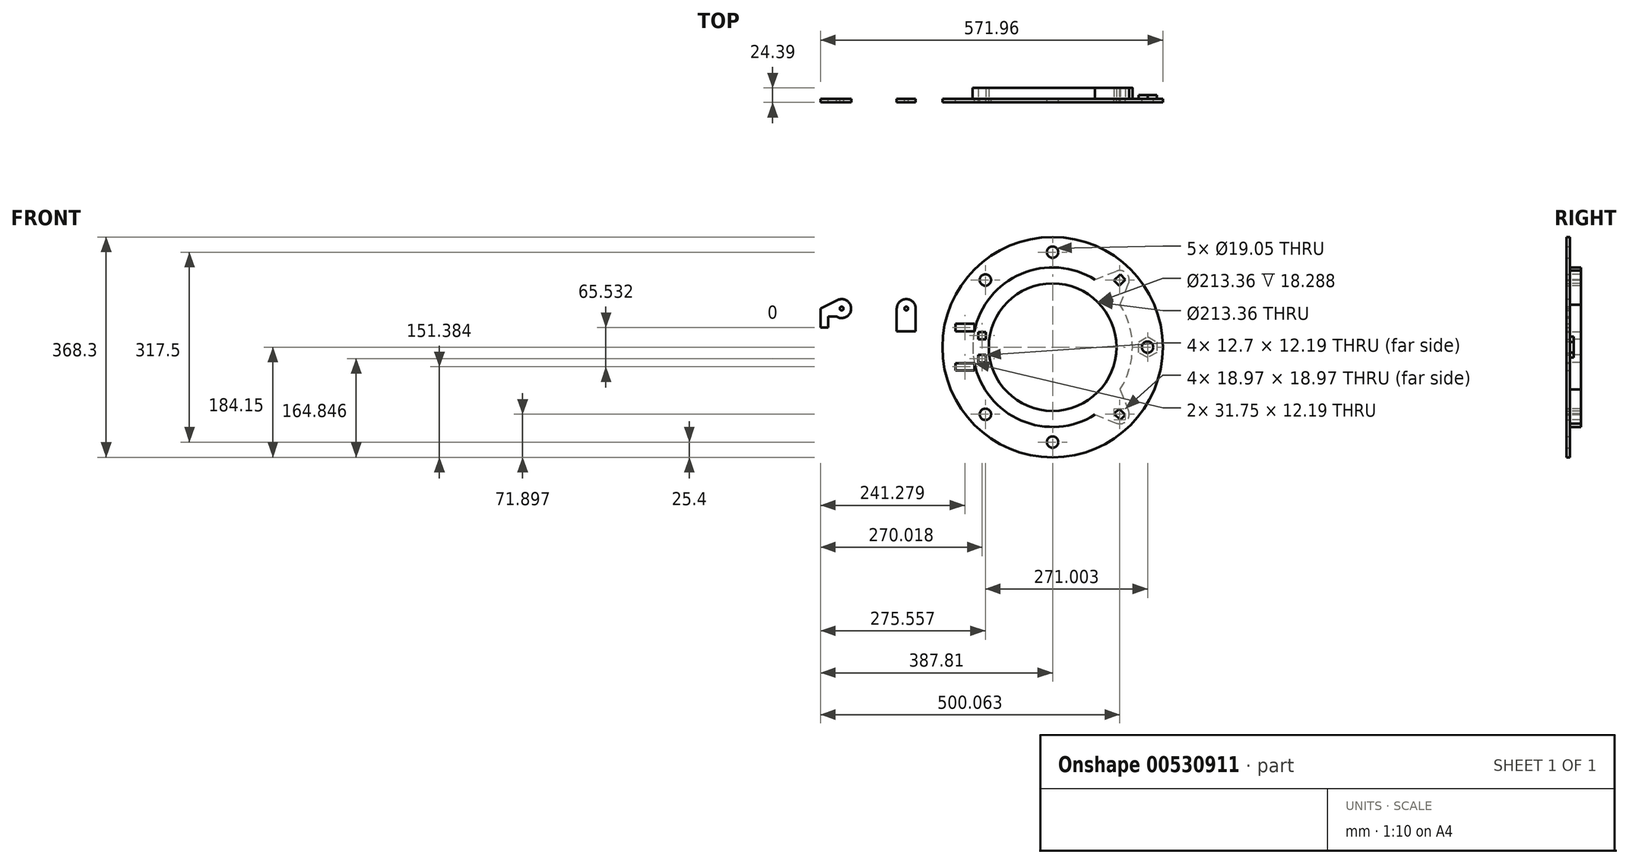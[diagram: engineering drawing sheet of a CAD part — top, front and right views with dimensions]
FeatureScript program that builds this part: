
annotation { "Feature Type Name" : "Feature", "Feature Type Description" : "" }
export const myFeature = defineFeature(function(context is Context, id is Id, definition is map)
    precondition{}
    {
        {
            var Q0;
            Q0=qCreatedBy(makeId("Front.planeOp"),FACE);
            var sketch = newSketch(context, id + "F0", { "sketchPlane" : qUnion([Q0])});
            skCircle(sketch, "E0", {"center": v(0, 0) * mm, "radius": 114.3 * mm, "construction": true});
            skArc(sketch, "E1", {"start": v(70.98, 112.89) * mm, "mid": v(-133.35, 0) * mm, "end": v(70.98, -112.89) * mm});
            skCircle(sketch, "E2", {"center": v(0, 0) * mm, "radius": 184.15 * mm});
            skCircle(sketch, "E3", {"center": v(0, 158.75) * mm, "radius": 9.53 * mm});
            skLineSegment(sketch, "E4", {"start": v(0, 133.35) * mm, "end": v(0, 184.15) * mm, "construction": true});
            skCircle(sketch, "E5.1.0", {"center": v(-112.25, 112.25) * mm, "radius": 9.53 * mm});
            skCircle(sketch, "E5.3.0", {"center": v(-112.25, -112.25) * mm, "radius": 9.53 * mm});
            skCircle(sketch, "E5.4.0", {"center": v(0, -158.75) * mm, "radius": 9.52 * mm});
            skCircle(sketch, "E5.5.0", {"center": v(112.25, -112.25) * mm, "radius": 9.53 * mm, "construction": true});
            skCircle(sketch, "E5.6.0", {"center": v(158.75, 0) * mm, "radius": 9.53 * mm});
            skCircle(sketch, "E5.7.0", {"center": v(112.25, 112.25) * mm, "radius": 9.53 * mm, "construction": true});
            skLineSegment(sketch, "E6", {"start": v(-133.35, 0) * mm, "end": v(-184.15, 0) * mm, "construction": true});
            skLineSegment(sketch, "E7.bottom", {"start": v(-162.4, 38.86) * mm, "end": v(-130.66, 38.86) * mm});
            skLineSegment(sketch, "E7.top", {"start": v(-162.4, 26.67) * mm, "end": v(-130.66, 26.67) * mm});
            skLineSegment(sketch, "E7.left", {"start": v(-162.4, 38.86) * mm, "end": v(-162.4, 26.67) * mm});
            skLineSegment(sketch, "E7.right", {"start": v(-130.66, 38.86) * mm, "end": v(-130.66, 26.67) * mm});
            skLineSegment(sketch, "E8.MirrorCS", {"start": v(-130.66, -38.86) * mm, "end": v(-130.66, -26.67) * mm});
            skLineSegment(sketch, "E9.MirrorCS", {"start": v(-162.4, -38.86) * mm, "end": v(-162.4, -26.67) * mm});
            skLineSegment(sketch, "E10.MirrorCS", {"start": v(-162.4, -26.67) * mm, "end": v(-130.66, -26.67) * mm});
            skLineSegment(sketch, "E11.MirrorCS", {"start": v(-162.4, -38.86) * mm, "end": v(-130.66, -38.86) * mm});
            skLineSegment(sketch, "E12", {"start": v(-228.6, 26.67) * mm, "end": v(-260.35, 26.67) * mm});
            skLineSegment(sketch, "E13", {"start": v(-260.35, 26.67) * mm, "end": v(-260.35, 64.52) * mm});
            skArc(sketch, "E14", {"start": v(-228.6, 64.52) * mm, "mid": v(-244.47, 80.4) * mm, "end": v(-260.35, 64.52) * mm});
            skPoint(sketch, "E14.centerSnap0", {"position": v(-244.48, 26.67) * mm});
            skLineSegment(sketch, "E15", {"start": v(-228.6, 26.67) * mm, "end": v(-228.6, 64.52) * mm});
            skLineSegment(sketch, "E16.bottom", {"start": v(-228.6, 26.67) * mm, "end": v(-203.2, 26.67) * mm, "construction": true});
            skLineSegment(sketch, "E16.top", {"start": v(-228.6, 51.05) * mm, "end": v(-203.2, 51.05) * mm, "construction": true});
            skLineSegment(sketch, "E16.left", {"start": v(-228.6, 26.67) * mm, "end": v(-228.6, 51.05) * mm, "construction": true});
            skLineSegment(sketch, "E16.right", {"start": v(-203.2, 26.67) * mm, "end": v(-203.2, 51.05) * mm, "construction": true});
            skLineSegment(sketch, "E17", {"start": v(-298.45, 64.52) * mm, "end": v(-298.45, 26.67) * mm, "construction": true});
            skLineSegment(sketch, "E18.MirrorCS", {"start": v(-368.3, 26.67) * mm, "end": v(-368.3, 64.52) * mm, "construction": true});
            skLineSegment(sketch, "E19.MirrorCS", {"start": v(-368.3, 26.67) * mm, "end": v(-368.3, 51.05) * mm, "construction": true});
            skLineSegment(sketch, "E20.MirrorCS", {"start": v(-368.3, 26.67) * mm, "end": v(-336.55, 26.67) * mm, "construction": true});
            skArc(sketch, "E21.MirrorCS", {"start": v(-359.55, 78.7) * mm, "mid": v(-344.09, 78.03) * mm, "end": v(-336.55, 64.52) * mm, "construction": true});
            skLineSegment(sketch, "E22.MirrorCS", {"start": v(-368.3, 51.05) * mm, "end": v(-393.7, 51.05) * mm, "construction": true});
            skLineSegment(sketch, "E23.MirrorCS", {"start": v(-393.7, 26.67) * mm, "end": v(-393.7, 51.05) * mm, "construction": true});
            skLineSegment(sketch, "E24.MirrorCS", {"start": v(-336.55, 26.67) * mm, "end": v(-336.55, 64.52) * mm, "construction": true});
            skPoint(sketch, "E25.MirrorP", {"position": v(-352.43, 26.67) * mm});
            skLineSegment(sketch, "E26.MirrorCS", {"start": v(-368.3, 26.67) * mm, "end": v(-393.7, 26.67) * mm, "construction": true});
            skArc(sketch, "E27", {"start": v(-360.84, 51.05) * mm, "mid": v(-336.57, 63.78) * mm, "end": v(-359.55, 78.7) * mm});
            skLineSegment(sketch, "E28", {"start": v(-130.66, 26.67) * mm, "end": v(-111.14, 26.67) * mm, "construction": true});
            skLineSegment(sketch, "E29", {"start": v(-368.3, 64.52) * mm, "end": v(-387.81, 64.52) * mm, "construction": true});
            skLineSegment(sketch, "E30", {"start": v(-387.81, 51.05) * mm, "end": v(-387.81, 64.52) * mm});
            skLineSegment(sketch, "E31", {"start": v(-387.81, 64.52) * mm, "end": v(-359.55, 78.7) * mm});
            skLineSegment(sketch, "E32", {"start": v(-387.81, 51.05) * mm, "end": v(-387.81, 32.77) * mm});
            skLineSegment(sketch, "E33", {"start": v(-387.81, 32.77) * mm, "end": v(-375.24, 32.77) * mm});
            skLineSegment(sketch, "E34", {"start": v(-375.24, 32.77) * mm, "end": v(-375.24, 51.05) * mm});
            skLineSegment(sketch, "E35", {"start": v(-375.24, 51.05) * mm, "end": v(-360.84, 51.05) * mm});
            skCircle(sketch, "E36.0", {"center": v(0, 0) * mm, "radius": 106.68 * mm});
            skLineSegment(sketch, "E37.bottom", {"start": v(-111.44, 25.4) * mm, "end": v(-124.14, 25.4) * mm});
            skLineSegment(sketch, "E37.top", {"start": v(-111.44, 13.2) * mm, "end": v(-124.14, 13.2) * mm});
            skLineSegment(sketch, "E37.left", {"start": v(-111.44, 25.4) * mm, "end": v(-111.44, 13.2) * mm});
            skLineSegment(sketch, "E37.right", {"start": v(-124.14, 25.4) * mm, "end": v(-124.14, 13.2) * mm});
            skLineSegment(sketch, "E38", {"start": v(0, 0) * mm, "end": v(112.25, 112.25) * mm, "construction": true});
            skLineSegment(sketch, "E39", {"start": v(0, 0) * mm, "end": v(112.25, -112.25) * mm, "construction": true});
            skArc(sketch, "E40", {"start": v(127, 106.37) * mm, "mid": v(123.48, 123.48) * mm, "end": v(106.37, 127) * mm});
            skLineSegment(sketch, "E41", {"start": v(70.98, 112.89) * mm, "end": v(106.37, 127) * mm});
            skLineSegment(sketch, "E42.MirrorCS", {"start": v(112.89, 70.98) * mm, "end": v(127, 106.37) * mm});
            skLineSegment(sketch, "E43.MirrorCS", {"start": v(70.98, -112.89) * mm, "end": v(106.37, -127) * mm});
            skArc(sketch, "E44.MirrorCS", {"start": v(127, -106.37) * mm, "mid": v(123.48, -123.48) * mm, "end": v(106.37, -127) * mm});
            skLineSegment(sketch, "E45.MirrorCS", {"start": v(112.89, -70.98) * mm, "end": v(127, -106.37) * mm});
            skArc(sketch, "E46.trimOffspring", {"start": v(112.89, -70.98) * mm, "mid": v(133.35, 0) * mm, "end": v(112.89, 70.98) * mm});
            skCircle(sketch, "E47.cCircle", {"center": v(158.75, 0) * mm, "radius": 15.24 * mm, "construction": true});
            skLineSegment(sketch, "E47.0", {"start": v(174, 8.8) * mm, "end": v(174, -8.8) * mm});
            skLineSegment(sketch, "E47.1", {"start": v(174, -8.8) * mm, "end": v(158.75, -17.6) * mm});
            skLineSegment(sketch, "E47.2", {"start": v(158.75, -17.6) * mm, "end": v(143.5, -8.8) * mm});
            skLineSegment(sketch, "E47.3", {"start": v(143.5, -8.8) * mm, "end": v(143.5, 8.8) * mm});
            skLineSegment(sketch, "E47.4", {"start": v(143.5, 8.8) * mm, "end": v(158.75, 17.6) * mm});
            skLineSegment(sketch, "E47.5", {"start": v(158.75, 17.6) * mm, "end": v(174, 8.8) * mm});
            skPoint(sketch, "E47.0.midPoint", {"position": v(174, 0) * mm});
            skArc(sketch, "E48", {"start": v(70.98, 112.89) * mm, "mid": v(94.3, 94.3) * mm, "end": v(112.89, 70.98) * mm});
            skArc(sketch, "E49", {"start": v(70.98, -112.89) * mm, "mid": v(94.3, -94.3) * mm, "end": v(112.89, -70.98) * mm});
            skLineSegment(sketch, "E50.MirrorCS", {"start": v(-124.14, -25.4) * mm, "end": v(-124.14, -13.2) * mm});
            skLineSegment(sketch, "E51.MirrorCS", {"start": v(-111.44, -25.4) * mm, "end": v(-111.44, -13.2) * mm});
            skLineSegment(sketch, "E52.MirrorCS", {"start": v(-111.44, -25.4) * mm, "end": v(-124.14, -25.4) * mm});
            skLineSegment(sketch, "E53.MirrorCS", {"start": v(-111.44, -13.2) * mm, "end": v(-124.14, -13.2) * mm});
            skLineSegment(sketch, "E54", {"start": v(102.77, 111.39) * mm, "end": v(111.39, 102.77) * mm});
            skLineSegment(sketch, "E55", {"start": v(102.77, 111.39) * mm, "end": v(113.12, 121.74) * mm});
            skLineSegment(sketch, "E56", {"start": v(113.12, 121.74) * mm, "end": v(121.74, 113.12) * mm});
            skLineSegment(sketch, "E57", {"start": v(121.74, 113.12) * mm, "end": v(111.39, 102.77) * mm});
            skLineSegment(sketch, "E58.MirrorCS", {"start": v(113.12, -121.74) * mm, "end": v(121.74, -113.12) * mm});
            skLineSegment(sketch, "E59.MirrorCS", {"start": v(102.77, -111.39) * mm, "end": v(113.12, -121.74) * mm});
            skLineSegment(sketch, "E60", {"start": v(102.77, -111.39) * mm, "end": v(111.39, -102.77) * mm});
            skLineSegment(sketch, "E61", {"start": v(111.39, -102.77) * mm, "end": v(121.74, -113.12) * mm});
            skLineSegment(sketch, "E62.bottom", {"start": v(152.4, 176.78) * mm, "end": v(166.62, 176.78) * mm});
            skLineSegment(sketch, "E62.top", {"start": v(152.4, 152.4) * mm, "end": v(166.62, 152.4) * mm});
            skLineSegment(sketch, "E62.left", {"start": v(152.4, 176.78) * mm, "end": v(152.4, 152.4) * mm});
            skLineSegment(sketch, "E62.right", {"start": v(166.62, 176.78) * mm, "end": v(166.62, 152.4) * mm});
            skLineSegment(sketch, "E63", {"start": v(166.62, 176.78) * mm, "end": v(204.72, 202.18) * mm});
            skLineSegment(sketch, "E64", {"start": v(159.51, 176.78) * mm, "end": v(159.51, 152.4) * mm, "construction": true});
            skLineSegment(sketch, "E65", {"start": v(204.72, 202.18) * mm, "end": v(204.72, 214.88) * mm});
            skLineSegment(sketch, "E66", {"start": v(204.72, 214.88) * mm, "end": v(179.32, 214.88) * mm});
            skLineSegment(sketch, "E67", {"start": v(179.32, 214.88) * mm, "end": v(159.51, 201.68) * mm});
            skLineSegment(sketch, "E68.MirrorCS", {"start": v(139.7, 214.88) * mm, "end": v(159.51, 201.68) * mm});
            skLineSegment(sketch, "E69.MirrorCS", {"start": v(114.3, 214.88) * mm, "end": v(139.7, 214.88) * mm});
            skLineSegment(sketch, "E70.MirrorCS", {"start": v(114.3, 202.18) * mm, "end": v(114.3, 214.88) * mm});
            skLineSegment(sketch, "E71.MirrorCS", {"start": v(152.4, 176.78) * mm, "end": v(114.3, 202.18) * mm});
            skCircle(sketch, "E72", {"center": v(-244.47, 64.52) * mm, "radius": 3.18 * mm});
            skCircle(sketch, "E73", {"center": v(-352.43, 64.52) * mm, "radius": 3.18 * mm});
            skSolve(sketch);
        }
        {
            var Q0;
            Q0=makeQuery(id+"F0.imprint","IMPRINT",FACE,{"disambiguationData":[TD([[makeQuery(id+"F0.imprint","IMPRINT",EDGE,{"derivedFrom":sQuery(id+"F0.wireOp",EDGE,"E30")}),-1.0]])]});
            var Q1;
            {var subQ0=sQuery(id+"F0.wireOp",EDGE,"E27");var subQ1=makeQuery(id+"F0.imprint","INTERSECT",VERTEX,{"derivedFrom":[subQ0,sQuery(id+"F0.wireOp",EDGE,"E31")]});Q1=makeQuery(id+"F0.imprint","IMPRINT",FACE,{"disambiguationData":[TD([[makeQuery(id+"F0.imprint","IMPRINT",EDGE,{"disambiguationData":[TD([[subQ1,-1.0]])],"derivedFrom":subQ0}),1.0]])]});}
            var Q2;
            Q2=makeQuery(id+"F0.imprint","IMPRINT",FACE,{"disambiguationData":[TD([[makeQuery(id+"F0.imprint","IMPRINT",EDGE,{"derivedFrom":sQuery(id+"F0.wireOp",EDGE,"E12")}),-1.0]])]});
            var Q3;
            Q3=makeQuery(id+"F0.imprint","IMPRINT",FACE,{"disambiguationData":[TD([[makeQuery(id+"F0.imprint","IMPRINT",EDGE,{"derivedFrom":sQuery(id+"F0.wireOp",EDGE,"E2")}),1.0]])]});
            var Q4;
            Q4=makeQuery(id+"F0.imprint","IMPRINT",FACE,{"disambiguationData":[TD([[makeQuery(id+"F0.imprint","IMPRINT",EDGE,{"derivedFrom":sQuery(id+"F0.wireOp",EDGE,"E36.0")}),-1.0]])]});
            var Q5;
            Q5=makeQuery(id+"F0.imprint","IMPRINT",FACE,{"disambiguationData":[TD([[makeQuery(id+"F0.imprint","IMPRINT",EDGE,{"derivedFrom":sQuery(id+"F0.wireOp",EDGE,"E40")}),1.0]])]});
            var Q6;
            Q6=makeQuery(id+"F0.imprint","IMPRINT",FACE,{"disambiguationData":[TD([[makeQuery(id+"F0.imprint","IMPRINT",EDGE,{"derivedFrom":sQuery(id+"F0.wireOp",EDGE,"E43.MirrorCS")}),1.0]])]});
            var Q7;
            Q7=makeQuery(id+"F0.imprint","IMPRINT",FACE,{"disambiguationData":[TD([[makeQuery(id+"F0.imprint","IMPRINT",EDGE,{"derivedFrom":sQuery(id+"F0.wireOp",EDGE,"E5.6.0")}),-1.0]])]});
            extrude(context, id + "F1", {"entities" : qUnion([Q0, Q1, Q2, Q3, Q4, Q5, Q6, Q7]), "depth" : 6.1 * mm, "offsetDistance" : 25.4 * mm});
        }
        {
            var Q0;
            Q0=makeQuery(id+"F0.imprint","IMPRINT",FACE,{"disambiguationData":[TD([[makeQuery(id+"F0.imprint","IMPRINT",EDGE,{"derivedFrom":sQuery(id+"F0.wireOp",EDGE,"E36.0")}),-1.0]])]});
            var Q1;
            Q1=makeQuery(id+"F0.imprint","IMPRINT",FACE,{"disambiguationData":[TD([[makeQuery(id+"F0.imprint","IMPRINT",EDGE,{"derivedFrom":sQuery(id+"F0.wireOp",EDGE,"E40")}),1.0]])]});
            var Q2;
            Q2=makeQuery(id+"F0.imprint","IMPRINT",FACE,{"disambiguationData":[TD([[makeQuery(id+"F0.imprint","IMPRINT",EDGE,{"derivedFrom":sQuery(id+"F0.wireOp",EDGE,"E43.MirrorCS")}),1.0]])]});
            extrude(context, id + "F2", {"entities" : qUnion([Q0, Q1, Q2]), "oppositeDirection" : true, "depth" : 18.29 * mm, "offsetDistance" : 25.4 * mm});
        }
        {
            var Q0;
            Q0=makeQuery(id+"F0.imprint","IMPRINT",FACE,{"disambiguationData":[TD([[makeQuery(id+"F0.imprint","IMPRINT",EDGE,{"derivedFrom":sQuery(id+"F0.wireOp",EDGE,"E5.6.0")}),-1.0]])]});
            var Q1;
            Q1=makeQuery(id+"F0.imprint","IMPRINT",FACE,{"disambiguationData":[TD([[makeQuery(id+"F0.imprint","IMPRINT",EDGE,{"derivedFrom":sQuery(id+"F0.wireOp",EDGE,"E5.6.0")}),1.0]])]});
            extrude(context, id + "F3", {"entities" : qUnion([Q0, Q1]), "oppositeDirection" : true, "depth" : 6.1 * mm, "offsetDistance" : 25.4 * mm});
        }
    });
